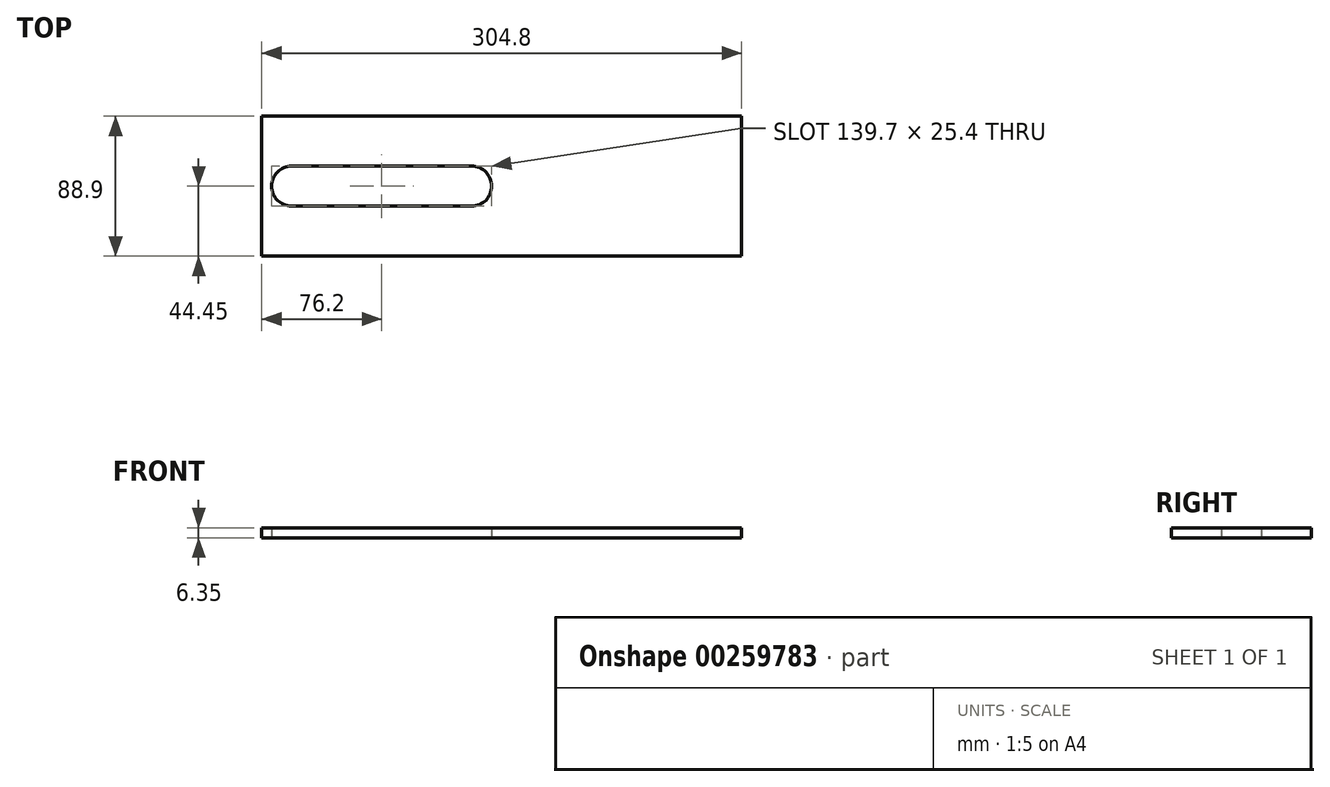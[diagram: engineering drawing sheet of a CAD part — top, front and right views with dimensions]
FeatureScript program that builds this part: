
annotation { "Feature Type Name" : "Feature", "Feature Type Description" : "" }
export const myFeature = defineFeature(function(context is Context, id is Id, definition is map)
    precondition{}
    {
        {
            var Q0;
            Q0=qCreatedBy(makeId("Top.planeOp"),FACE);
            var sketch = newSketch(context, id + "F0", { "sketchPlane" : qUnion([Q0])});
            skLineSegment(sketch, "E0.bottom", {"start": v(152.4, -44.45) * mm, "end": v(-152.4, -44.45) * mm});
            skLineSegment(sketch, "E0.top", {"start": v(152.4, 44.45) * mm, "end": v(-152.4, 44.45) * mm});
            skLineSegment(sketch, "E0.left", {"start": v(152.4, -44.45) * mm, "end": v(152.4, 44.45) * mm});
            skLineSegment(sketch, "E0.right", {"start": v(-152.4, -44.45) * mm, "end": v(-152.4, 44.45) * mm});
            skPoint(sketch, "E0.middle", {"position": v(0, 0) * mm});
            skLineSegment(sketch, "E1", {"start": v(-133.35, 0) * mm, "end": v(-19.05, 0) * mm, "construction": true});
            skLineSegment(sketch, "E2", {"start": v(-133.35, 12.7) * mm, "end": v(-133.35, 12.7) * mm});
            skLineSegment(sketch, "E3", {"start": v(-133.35, -12.7) * mm, "end": v(-133.35, -12.7) * mm});
            skLineSegment(sketch, "E4", {"start": v(-133.35, 0) * mm, "end": v(-133.35, -12.7) * mm, "construction": true});
            skLineSegment(sketch, "E5", {"start": v(-133.35, 0) * mm, "end": v(-133.35, 12.7) * mm, "construction": true});
            skLineSegment(sketch, "E6", {"start": v(-19.05, 0) * mm, "end": v(-19.05, 12.7) * mm, "construction": true});
            skLineSegment(sketch, "E7", {"start": v(-19.05, 0) * mm, "end": v(-19.05, -12.7) * mm, "construction": true});
            skLineSegment(sketch, "E8", {"start": v(-133.35, 12.7) * mm, "end": v(-19.05, 12.7) * mm});
            skLineSegment(sketch, "E9", {"start": v(-133.35, -12.7) * mm, "end": v(-19.05, -12.7) * mm});
            skArc(sketch, "E10", {"start": v(-133.35, 12.7) * mm, "mid": v(-146.05, 0) * mm, "end": v(-133.35, -12.7) * mm});
            skArc(sketch, "E11", {"start": v(-19.05, -12.7) * mm, "mid": v(-6.35, 0) * mm, "end": v(-19.05, 12.7) * mm});
            skSolve(sketch);
        }
        {
            var Q0;
            Q0 = qSketchRegion(id + "F0", true);
            extrude(context, id + "F1", {"entities" : qUnion([Q0]), "depth" : 6.35 * mm});
        }
    });
